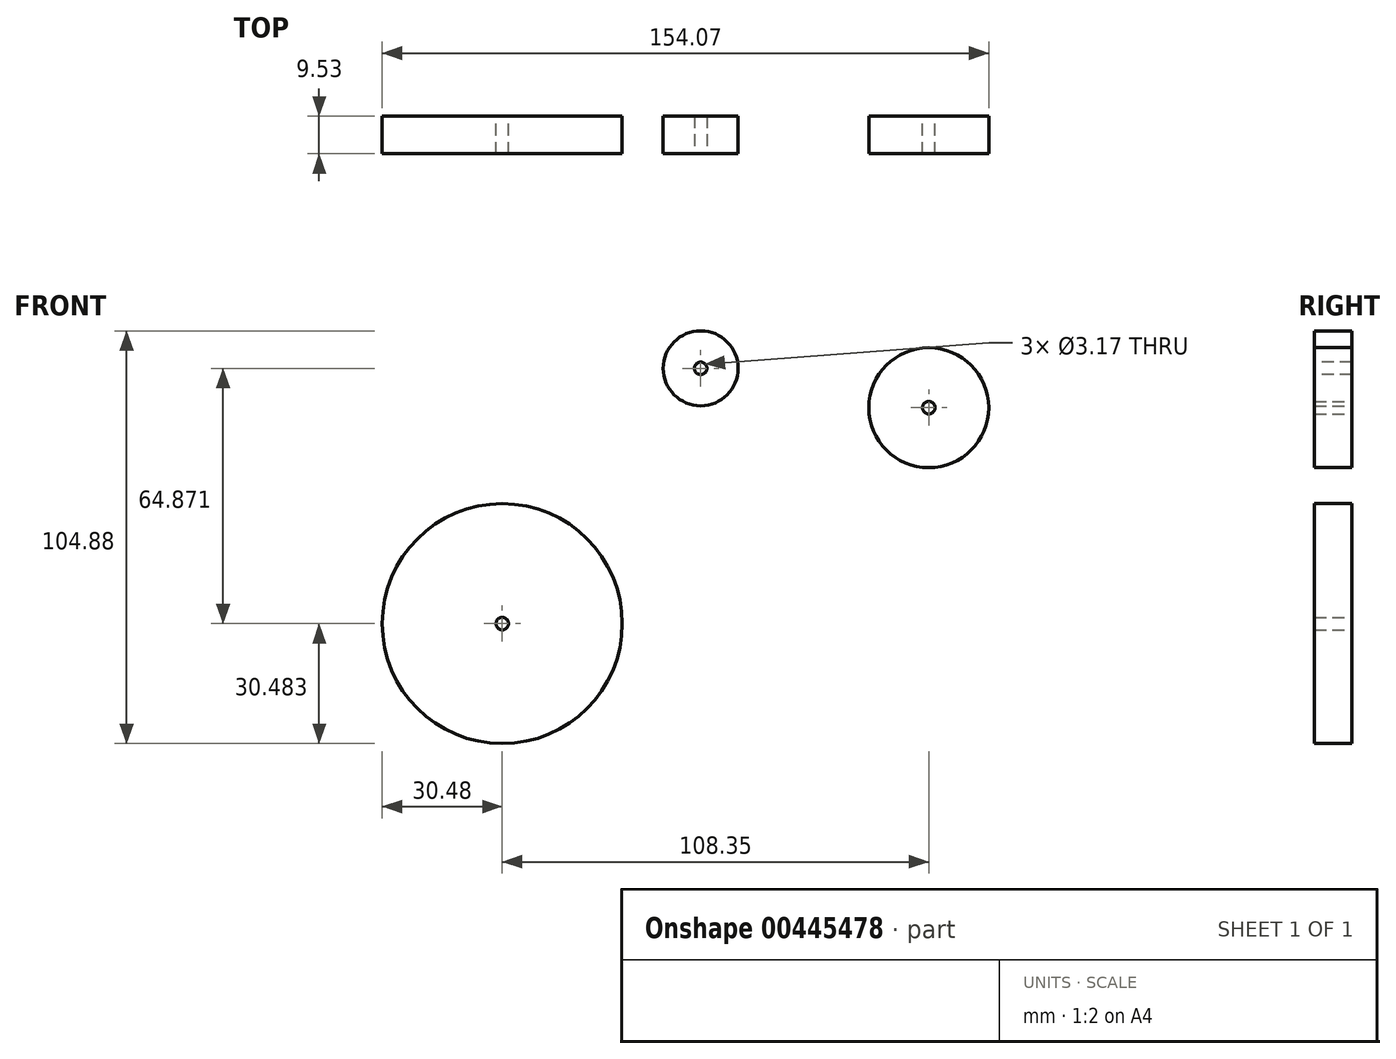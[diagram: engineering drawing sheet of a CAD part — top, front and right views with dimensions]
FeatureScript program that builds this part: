
annotation { "Feature Type Name" : "Feature", "Feature Type Description" : "" }
export const myFeature = defineFeature(function(context is Context, id is Id, definition is map)
    precondition{}
    {
        {
            var Q0;
            Q0=qCreatedBy(makeId("Front.planeOp"),FACE);
            var sketch = newSketch(context, id + "F0", { "sketchPlane" : qUnion([Q0])});
            skCircle(sketch, "E0", {"center": v(-45.75, 21.07) * mm, "radius": 9.53 * mm});
            skSolve(sketch);
        }
        {
            var Q0;
            Q0=makeQuery(id+"F0.imprint","IMPRINT",FACE,{"disambiguationData":[TD([[makeQuery(id+"F0.imprint","IMPRINT",EDGE,{"derivedFrom":sQuery(id+"F0.wireOp",EDGE,"E0")}),1.0]])]});
            extrude(context, id + "F1", {"entities" : qUnion([Q0]), "depth" : 9.52 * mm});
        }
        {
            var Q0;
            Q0=qCreatedBy(makeId("Front.planeOp"),FACE);
            var sketch = newSketch(context, id + "F2", { "sketchPlane" : qUnion([Q0])});
            skCircle(sketch, "E1", {"center": v(12.18, 11.07) * mm, "radius": 15.24 * mm});
            skCircle(sketch, "E2", {"center": v(-96.17, -43.8) * mm, "radius": 30.48 * mm});
            skCircle(sketch, "E3", {"center": v(-96.17, -43.8) * mm, "radius": 1.59 * mm});
            skCircle(sketch, "E4", {"center": v(12.18, 11.07) * mm, "radius": 1.59 * mm});
            skSolve(sketch);
        }
        {
            var Q0;
            Q0 = qSketchRegion(id + "F2", true);
            extrude(context, id + "F3", {"entities" : qUnion([Q0]), "depth" : 9.52 * mm, "offsetDistance" : 25.4 * mm});
        }
        {
            var Q0;
            Q0=makeQuery(id+"F1.opExtrude","CAP_FACE",FACE,{"disambiguationData":[OSD([sQuery(id+"F0.wireOp",EDGE,"E0")])],"isStart":false});
            var sketch = newSketch(context, id + "F4", { "sketchPlane" : qUnion([Q0])});
            skCircle(sketch, "E5", {"center": v(-45.75, 21.07) * mm, "radius": 1.59 * mm});
            skSolve(sketch);
        }
        {
            var Q0;
            Q0 = qSketchRegion(id + "F4", true);
            extrude(context, id + "F5", {"entities" : qUnion([Q0]), "operationType" : NewBodyOperationType.REMOVE, "oppositeDirection" : true, "depth" : 25.4 * mm, "offsetDistance" : 25.4 * mm});
        }
    });
